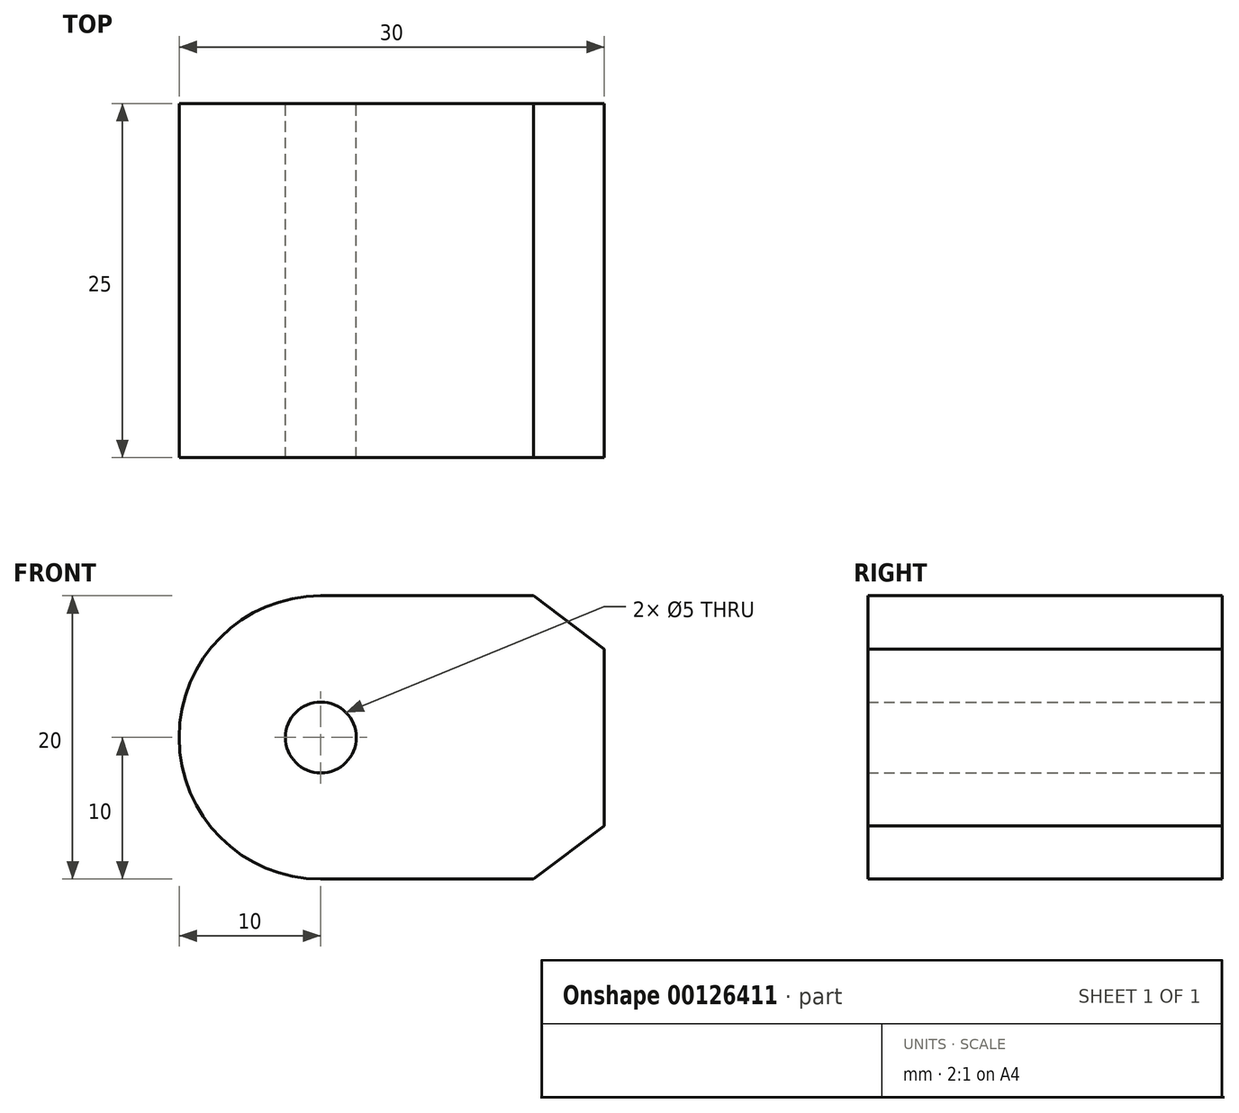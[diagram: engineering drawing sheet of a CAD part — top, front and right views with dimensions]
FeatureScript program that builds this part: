
annotation { "Feature Type Name" : "Feature", "Feature Type Description" : "" }
export const myFeature = defineFeature(function(context is Context, id is Id, definition is map)
    precondition{}
    {
        {
            var Q0;
            Q0=qCreatedBy(makeId("Front.planeOp"),FACE);
            var sketch = newSketch(context, id + "F0", { "sketchPlane" : qUnion([Q0])});
            skCircle(sketch, "E0", {"center": v(0, 0) * mm, "radius": 2.5 * mm});
            skArc(sketch, "E1", {"start": v(9.68, 2.5) * mm, "mid": v(-10, 0) * mm, "end": v(9.68, -2.5) * mm});
            skLineSegment(sketch, "E2", {"start": v(0, 10) * mm, "end": v(15, 10) * mm});
            skLineSegment(sketch, "E3", {"start": v(15, 10) * mm, "end": v(20, 6.25) * mm});
            skLineSegment(sketch, "E4", {"start": v(20, 6.25) * mm, "end": v(20, -6.25) * mm});
            skLineSegment(sketch, "E5", {"start": v(20, -6.25) * mm, "end": v(15, -10) * mm});
            skLineSegment(sketch, "E6", {"start": v(15, -10) * mm, "end": v(0, -10) * mm});
            skSolve(sketch);
        }
        {
            var Q0;
            Q0 = qSketchRegion(id + "F0", true);
            extrude(context, id + "F1", {"entities" : qUnion([Q0]), "depth" : 25 * mm});
        }
    });
